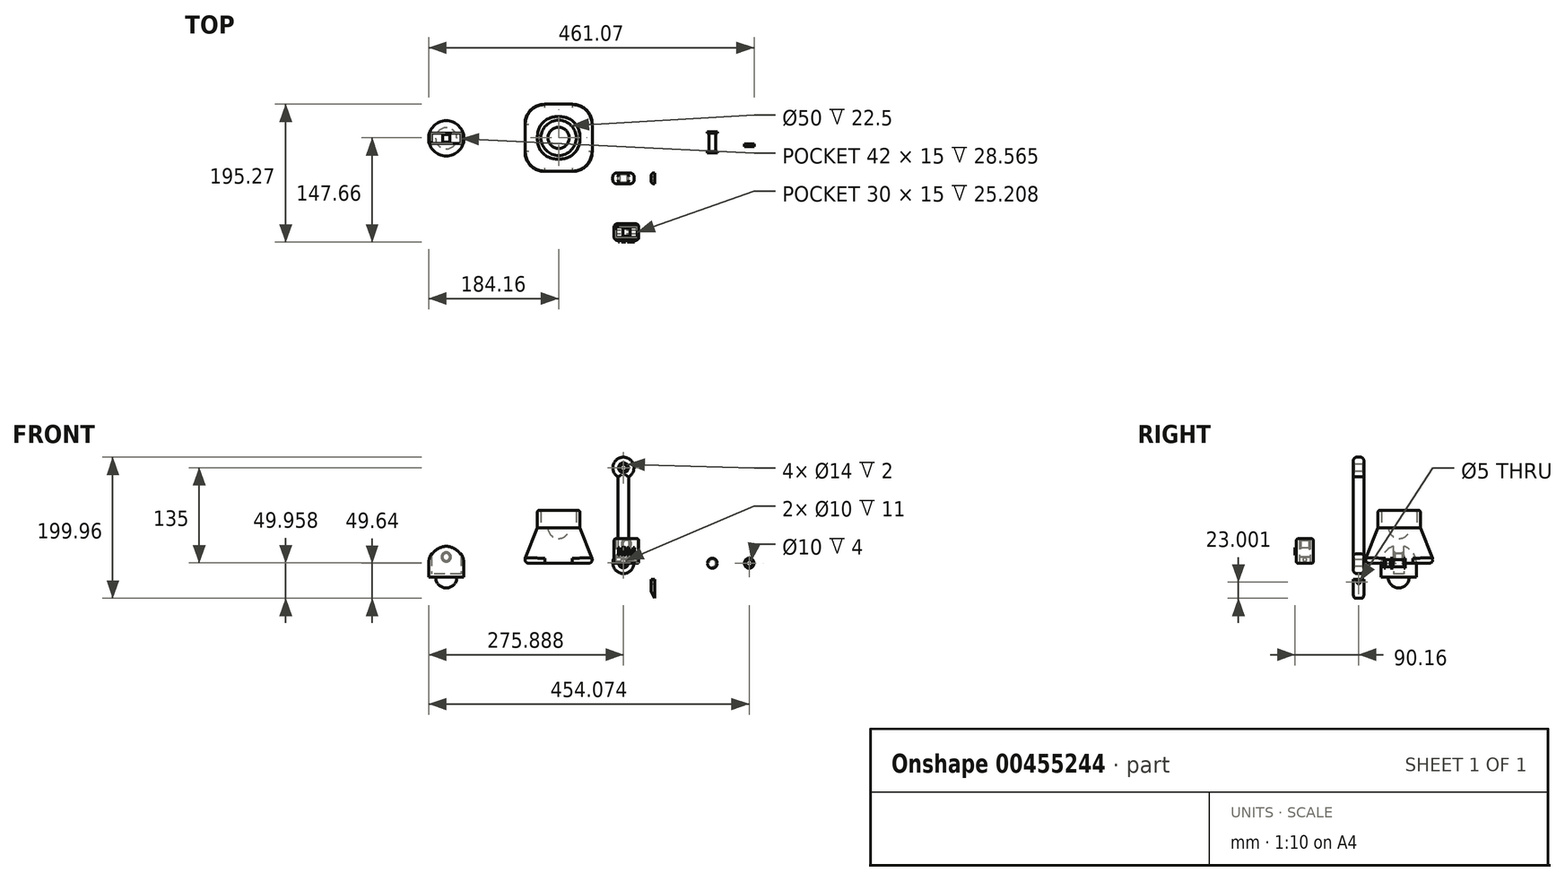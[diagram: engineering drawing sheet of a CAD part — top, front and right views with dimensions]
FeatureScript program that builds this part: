
annotation { "Feature Type Name" : "Feature", "Feature Type Description" : "" }
export const myFeature = defineFeature(function(context is Context, id is Id, definition is map)
    precondition{}
    {
        {
            var Q0;
            Q0=qCreatedBy(makeId("Top.planeOp"),FACE);
            var sketch = newSketch(context, id + "F0", { "sketchPlane" : qUnion([Q0])});
            skLineSegment(sketch, "E0.bottom", {"start": v(0, 0) * mm, "end": v(100, 0) * mm});
            skLineSegment(sketch, "E0.top", {"start": v(0, 100) * mm, "end": v(100, 100) * mm});
            skLineSegment(sketch, "E0.left", {"start": v(0, 0) * mm, "end": v(0, 100) * mm});
            skLineSegment(sketch, "E0.right", {"start": v(100, 0) * mm, "end": v(100, 100) * mm});
            skSolve(sketch);
        }
        {
            var Q0;
            Q0=makeQuery(id+"F0.imprint","IMPRINT",FACE,{"disambiguationData":[TD([[makeQuery(id+"F0.imprint","IMPRINT",EDGE,{"derivedFrom":sQuery(id+"F0.wireOp",EDGE,"E0.bottom")}),1.0]])]});
            cPlane(context, id + "F1", {"entities" : qUnion([Q0]), "cplaneType" : CPlaneType.OFFSET, "offset" : 50 * mm, "width" : 150 * mm, "height" : 150 * mm});
        }
        {
            var Q0;
            Q0=qCreatedBy(id+"F1.planeOp",FACE);
            var sketch = newSketch(context, id + "F2", { "sketchPlane" : qUnion([Q0])});
            skLineSegment(sketch, "E1.bottom", {"start": v(20, 80) * mm, "end": v(80, 80) * mm});
            skLineSegment(sketch, "E1.top", {"start": v(20, 20) * mm, "end": v(80, 20) * mm});
            skLineSegment(sketch, "E1.left", {"start": v(20, 80) * mm, "end": v(20, 20) * mm});
            skLineSegment(sketch, "E1.right", {"start": v(80, 80) * mm, "end": v(80, 20) * mm});
            skSolve(sketch);
        }
        {
            var Q0;
            Q0=makeQuery(id+"F0.imprint","IMPRINT",FACE,{"disambiguationData":[TD([[makeQuery(id+"F0.imprint","IMPRINT",EDGE,{"derivedFrom":sQuery(id+"F0.wireOp",EDGE,"E0.bottom")}),1.0]])]});
            var Q1;
            Q1=makeQuery(id+"F2.imprint","IMPRINT",FACE,{"disambiguationData":[TD([[makeQuery(id+"F2.imprint","IMPRINT",EDGE,{"derivedFrom":sQuery(id+"F2.wireOp",EDGE,"E1.bottom")}),-1.0]])]});
            loft(context, id + "F3", {"sheetProfilesArray" : [{ "sheetProfileEntities" : qUnion([Q0]) }, { "sheetProfileEntities" : qUnion([Q1]) }]});
        }
        {
            var Q0;
            Q0=makeQuery(id+"F3.opLoft","CAP_FACE",FACE,{"disambiguationData":[OSD([makeQuery(id+"F2.imprint","IMPRINT",FACE,{"disambiguationData":[TD([[makeQuery(id+"F2.imprint","IMPRINT",EDGE,{"derivedFrom":sQuery(id+"F2.wireOp",EDGE,"E1.bottom")}),-1.0]])]})])],"isStart":true});
            var sketch = newSketch(context, id + "F4", { "sketchPlane" : qUnion([Q0])});
            skLineSegment(sketch, "E2", {"start": v(50, 65) * mm, "end": v(50, 35) * mm});
            skArc(sketch, "E3", {"start": v(50, 35) * mm, "mid": v(65, 50) * mm, "end": v(50, 65) * mm});
            skPoint(sketch, "E4.orphan", {"position": v(50, 80) * mm});
            skPoint(sketch, "E5.orphan", {"position": v(50, 20) * mm});
            skSolve(sketch);
        }
        {
            var Q0;
            Q0=makeQuery(id+"F4.imprint","IMPRINT",FACE,{"disambiguationData":[TD([[makeQuery(id+"F4.imprint","IMPRINT",EDGE,{"derivedFrom":sQuery(id+"F4.wireOp",EDGE,"E2")}),1.0]])]});
            var Q1;
            Q1=sQuery(id+"F4.wireOp",EDGE,"E2");
            revolve(context, id + "F5", {"operationType" : NewBodyOperationType.REMOVE, "entities" : qUnion([Q0]), "axis" : qUnion([Q1]), "revolveType" : RevolveType.FULL, "oppositeDirection" : true});
        }
        {
            var Q0;
            Q0=makeQuery(id+"F3.opLoft","CAP_FACE",FACE,{"disambiguationData":[OSD([makeQuery(id+"F0.imprint","IMPRINT",FACE,{"disambiguationData":[TD([[makeQuery(id+"F0.imprint","IMPRINT",EDGE,{"derivedFrom":sQuery(id+"F0.wireOp",EDGE,"E0.bottom")}),1.0]])]})])],"isStart":true});
            fillet(context, id + "F6", {"entities" : qUnion([Q0]), "radius" : 5 * mm, "tangentPropagation" : true, "allowEdgeOverflow" : false});
        }
        {
            var Q0;
            Q0=makeQuery(id+"F3.opLoft","SWEPT_EDGE",EDGE,{"disambiguationData":[OSD([sQuery(id+"F0.wireOp",EDGE,"E0.bottom"),sQuery(id+"F0.wireOp",EDGE,"E0.right"),sQuery(id+"F2.wireOp",EDGE,"E1.top"),sQuery(id+"F2.wireOp",EDGE,"E1.right")])]});
            var Q1;
            Q1=makeQuery(id+"F3.opLoft","SWEPT_EDGE",EDGE,{"disambiguationData":[OSD([sQuery(id+"F0.wireOp",EDGE,"E0.top"),sQuery(id+"F0.wireOp",EDGE,"E0.right"),sQuery(id+"F2.wireOp",EDGE,"E1.bottom"),sQuery(id+"F2.wireOp",EDGE,"E1.right")])]});
            var Q2;
            Q2=makeQuery(id+"F3.opLoft","SWEPT_EDGE",EDGE,{"disambiguationData":[OSD([sQuery(id+"F0.wireOp",EDGE,"E0.top"),sQuery(id+"F0.wireOp",EDGE,"E0.left"),sQuery(id+"F2.wireOp",EDGE,"E1.bottom"),sQuery(id+"F2.wireOp",EDGE,"E1.left")])]});
            var Q3;
            Q3=makeQuery(id+"F3.opLoft","SWEPT_EDGE",EDGE,{"disambiguationData":[OSD([sQuery(id+"F0.wireOp",EDGE,"E0.bottom"),sQuery(id+"F0.wireOp",EDGE,"E0.left"),sQuery(id+"F2.wireOp",EDGE,"E1.top"),sQuery(id+"F2.wireOp",EDGE,"E1.left")])]});
            fillet(context, id + "F7", {"entities" : qUnion([Q0, Q1, Q2, Q3]), "radius" : 30 * mm, "tangentPropagation" : true, "allowEdgeOverflow" : false});
        }
        {
            var Q0;
            Q0=qCreatedBy(makeId("Top.planeOp"),FACE);
            var sketch = newSketch(context, id + "F8", { "sketchPlane" : qUnion([Q0])});
            skArc(sketch, "E6", {"start": v(184.89, 22.61) * mm, "mid": v(199.89, 37.61) * mm, "end": v(184.89, 52.61) * mm});
            skLineSegment(sketch, "E7", {"start": v(184.89, 22.61) * mm, "end": v(184.89, 52.61) * mm});
            skSolve(sketch);
        }
        {
            var Q0;
            Q0=qCreatedBy(makeId("Top.planeOp"),FACE);
            cPlane(context, id + "F9", {"entities" : qUnion([Q0]), "cplaneType" : CPlaneType.OFFSET, "offset" : 10 * mm, "width" : 150 * mm, "height" : 150 * mm});
        }
        {
            var Q0;
            Q0=qCreatedBy(id+"F9.planeOp",FACE);
            var sketch = newSketch(context, id + "F10", { "sketchPlane" : qUnion([Q0])});
            skLineSegment(sketch, "E8.bottom", {"start": v(177.39, 45.11) * mm, "end": v(192.39, 45.11) * mm});
            skLineSegment(sketch, "E8.top", {"start": v(177.39, 30.11) * mm, "end": v(192.39, 30.11) * mm});
            skLineSegment(sketch, "E8.left", {"start": v(177.39, 45.11) * mm, "end": v(177.39, 30.11) * mm});
            skLineSegment(sketch, "E8.right", {"start": v(192.39, 45.11) * mm, "end": v(192.39, 30.11) * mm});
            skSolve(sketch);
        }
        {
            var Q0;
            Q0=makeQuery(id+"F8.imprint","IMPRINT",FACE,{"disambiguationData":[TD([[makeQuery(id+"F8.imprint","IMPRINT",EDGE,{"derivedFrom":sQuery(id+"F8.wireOp",EDGE,"E6")}),1.0]])]});
            var Q1;
            Q1=sQuery(id+"F8.wireOp",EDGE,"E7");
            revolve(context, id + "F11", {"entities" : qUnion([Q0]), "axis" : qUnion([Q1]), "revolveType" : RevolveType.FULL});
        }
        {
            var Q0;
            Q0=qSketchRegion(id+"F10",true);
            extrude(context, id + "F12", {"entities" : qUnion([Q0]), "operationType" : NewBodyOperationType.ADD, "depth" : 120 * mm});
        }
        {
            var Q0;
            Q0=makeQuery(id+"F12.boolean.opBoolean","INTERSECT",EDGE,{"derivedFrom":[makeQuery(id+"F11.opRevolve","SWEPT_FACE",FACE,{"disambiguationData":[OSD([sQuery(id+"F8.wireOp",EDGE,"E6")])]}),makeQuery(id+"F12.opExtrude","SWEPT_FACE",FACE,{"disambiguationData":[OSD([sQuery(id+"F10.wireOp",EDGE,"E8.right")])]})]});
            var Q1;
            Q1=makeQuery(id+"F12.boolean.opBoolean","INTERSECT",EDGE,{"derivedFrom":[makeQuery(id+"F11.opRevolve","SWEPT_FACE",FACE,{"disambiguationData":[OSD([sQuery(id+"F8.wireOp",EDGE,"E6")])]}),makeQuery(id+"F12.opExtrude","SWEPT_FACE",FACE,{"disambiguationData":[OSD([sQuery(id+"F10.wireOp",EDGE,"E8.top")])]})]});
            var Q2;
            Q2=makeQuery(id+"F12.boolean.opBoolean","INTERSECT",EDGE,{"derivedFrom":[makeQuery(id+"F11.opRevolve","SWEPT_FACE",FACE,{"disambiguationData":[OSD([sQuery(id+"F8.wireOp",EDGE,"E6")])]}),makeQuery(id+"F12.opExtrude","SWEPT_FACE",FACE,{"disambiguationData":[OSD([sQuery(id+"F10.wireOp",EDGE,"E8.bottom")])]})]});
            var Q3;
            Q3=makeQuery(id+"F12.boolean.opBoolean","INTERSECT",EDGE,{"derivedFrom":[makeQuery(id+"F11.opRevolve","SWEPT_FACE",FACE,{"disambiguationData":[OSD([sQuery(id+"F8.wireOp",EDGE,"E6")])]}),makeQuery(id+"F12.opExtrude","SWEPT_FACE",FACE,{"disambiguationData":[OSD([sQuery(id+"F10.wireOp",EDGE,"E8.left")])]})]});
            var Q4;
            Q4=makeQuery(id+"F12.opExtrude","SWEPT_EDGE",EDGE,{"disambiguationData":[OSD([sQuery(id+"F10.wireOp",EDGE,"E8.bottom"),sQuery(id+"F10.wireOp",EDGE,"E8.left")])]});
            var Q5;
            Q5=makeQuery(id+"F12.opExtrude","SWEPT_EDGE",EDGE,{"disambiguationData":[OSD([sQuery(id+"F10.wireOp",EDGE,"E8.bottom"),sQuery(id+"F10.wireOp",EDGE,"E8.right")])]});
            var Q6;
            Q6=makeQuery(id+"F12.opExtrude","SWEPT_EDGE",EDGE,{"disambiguationData":[OSD([sQuery(id+"F10.wireOp",EDGE,"E8.top"),sQuery(id+"F10.wireOp",EDGE,"E8.right")])]});
            var Q7;
            Q7=makeQuery(id+"F12.opExtrude","SWEPT_EDGE",EDGE,{"disambiguationData":[OSD([sQuery(id+"F10.wireOp",EDGE,"E8.top"),sQuery(id+"F10.wireOp",EDGE,"E8.left")])]});
            fillet(context, id + "F13", {"entities" : qUnion([Q0, Q1, Q2, Q3, Q4, Q5, Q6, Q7]), "radius" : 5 * mm, "tangentPropagation" : true, "allowEdgeOverflow" : false});
        }
        {
            var Q0;
            Q0=makeQuery(id+"F12.opExtrude","CAP_EDGE",EDGE,{"disambiguationData":[OSD([sQuery(id+"F10.wireOp",EDGE,"E8.right")])],"isStart":false});
            cPoint(context, id + "F14", {"entities" : qUnion([Q0]), "parameter" : 0.5});
        }
        {
            var Q0;
            Q0=makeQuery(id+"F12.opExtrude","CAP_EDGE",EDGE,{"disambiguationData":[OSD([sQuery(id+"F10.wireOp",EDGE,"E8.left")])],"isStart":false});
            cPoint(context, id + "F15", {"entities" : qUnion([Q0]), "parameter" : 0.5});
        }
        {
            var Q0;
            {var subQ0=makeQuery(id+"F12.opExtrude","SWEPT_FACE",FACE,{"disambiguationData":[OSD([sQuery(id+"F10.wireOp",EDGE,"E8.left")])]});Q0=makeQuery(id+"F13.opFillet","BLEND_EDGE",EDGE,{"blendedFrom":[makeQuery(id+"F12.boolean.opBoolean","INTERSECT",EDGE,{"derivedFrom":[makeQuery(id+"F11.opRevolve","SWEPT_FACE",FACE,{"disambiguationData":[OSD([sQuery(id+"F8.wireOp",EDGE,"E6")])]}),subQ0]}),subQ0],"blendedInto":[subQ0]});}
            cPoint(context, id + "F16", {"entities" : qUnion([Q0]), "parameter" : 0.5});
        }
        {
            var Q0;
            Q0=qCreatedBy(id+"F14",VERTEX);
            var Q1;
            Q1=qCreatedBy(id+"F15",VERTEX);
            var Q2;
            Q2=qCreatedBy(id+"F16",VERTEX);
            cPlane(context, id + "F17", {"entities" : qUnion([Q0, Q1, Q2]), "cplaneType" : CPlaneType.THREE_POINT, "offset" : 25 * mm, "width" : 150 * mm, "height" : 150 * mm});
        }
        {
            var Q0;
            Q0=qCreatedBy(id+"F17.planeOp",FACE);
            var sketch = newSketch(context, id + "F18", { "sketchPlane" : qUnion([Q0])});
            skCircle(sketch, "E9", {"center": v(-184.89, 137.5) * mm, "radius": 15 * mm});
            skSolve(sketch);
        }
        {
            var Q0;
            Q0=makeQuery(id+"F18.imprint","IMPRINT",FACE,{"disambiguationData":[TD([[makeQuery(id+"F18.imprint","IMPRINT",EDGE,{"derivedFrom":sQuery(id+"F18.wireOp",EDGE,"E9")}),1.0]])]});
            extrude(context, id + "F19", {"entities" : qUnion([Q0]), "operationType" : NewBodyOperationType.ADD, "endBound" : BoundingType.SYMMETRIC, "depth" : 15 * mm, "offsetDistance" : 25 * mm});
        }
        {
            var Q0;
            Q0=makeQuery(id+"F19.opExtrude","CAP_EDGE",EDGE,{"disambiguationData":[OSD([sQuery(id+"F18.wireOp",EDGE,"E9")])],"isStart":true});
            var Q1;
            Q1=makeQuery(id+"F19.opExtrude","CAP_EDGE",EDGE,{"disambiguationData":[OSD([sQuery(id+"F18.wireOp",EDGE,"E9")])],"isStart":false});
            fillet(context, id + "F20", {"entities" : qUnion([Q0, Q1]), "radius" : 5 * mm, "tangentPropagation" : true, "allowEdgeOverflow" : false});
        }
        {
            var Q0;
            Q0=makeQuery(id+"F19.boolean.opBoolean","MERGE",FACE,{"derivedFrom":[makeQuery(id+"F12.opExtrude","SWEPT_FACE",FACE,{"disambiguationData":[OSD([sQuery(id+"F10.wireOp",EDGE,"E8.top")])]}),makeQuery(id+"F19.opExtrude","CAP_FACE",FACE,{"disambiguationData":[OSD([sQuery(id+"F18.wireOp",EDGE,"E9")])],"isStart":true})]});
            var sketch = newSketch(context, id + "F21", { "sketchPlane" : qUnion([Q0])});
            skCircle(sketch, "E10", {"center": v(184.89, 137.5) * mm, "radius": 5 * mm});
            skCircle(sketch, "E11", {"center": v(184.89, 137.5) * mm, "radius": 7 * mm});
            skSolve(sketch);
        }
        {
            var Q0;
            Q0=sQuery(id+"F21.wireOp",VERTEX,"E10.center");
            var Q1;
            Q1=makeQuery(id+"F11.opRevolve","SWEPT_BODY",BODY,{"disambiguationData":[OSD([sQuery(id+"F8.wireOp",EDGE,"E6"),sQuery(id+"F8.wireOp",EDGE,"E7")])]});
            hole(context, id + "F22", {"style" : HoleStyle.SIMPLE, "endStyle" : HoleEndStyle.THROUGH, "holeDiameter" : 10 * mm, "tappedDepth" : 12 * mm, "tapClearance" : 3, "locations" : qUnion([Q0]), "scope" : qUnion([Q1])});
        }
        {
            var Q0;
            Q0=makeQuery(id+"F19.boolean.opBoolean","MERGE",FACE,{"derivedFrom":[makeQuery(id+"F12.opExtrude","SWEPT_FACE",FACE,{"disambiguationData":[OSD([sQuery(id+"F10.wireOp",EDGE,"E8.bottom")])]}),makeQuery(id+"F19.opExtrude","CAP_FACE",FACE,{"disambiguationData":[OSD([sQuery(id+"F18.wireOp",EDGE,"E9")])],"isStart":false})]});
            var sketch = newSketch(context, id + "F23", { "sketchPlane" : qUnion([Q0])});
            skCircle(sketch, "E12", {"center": v(-184.89, 137.5) * mm, "radius": 7 * mm});
            skSolve(sketch);
        }
        {
            var Q0;
            Q0=qSketchRegion(id+"F21",true);
            var Q1;
            Q1=qSketchRegion(id+"F23",true);
            extrude(context, id + "F24", {"entities" : qUnion([Q0, Q1]), "operationType" : NewBodyOperationType.REMOVE, "oppositeDirection" : true, "depth" : 2 * mm, "hasSecondDirection" : true, "secondDirectionOppositeDirection" : false, "secondDirectionDepth" : 2 * mm});
        }
        {
            var Q0;
            Q0=qCreatedBy(makeId("Top.planeOp"),FACE);
            var sketch = newSketch(context, id + "F25", { "sketchPlane" : qUnion([Q0])});
            skLineSegment(sketch, "E13.bottom", {"start": v(267.71, 58.7) * mm, "end": v(272.71, 58.7) * mm});
            skLineSegment(sketch, "E13.top", {"start": v(267.71, 28.7) * mm, "end": v(272.71, 28.7) * mm});
            skLineSegment(sketch, "E13.left", {"start": v(267.71, 58.7) * mm, "end": v(267.71, 28.7) * mm});
            skLineSegment(sketch, "E13.right", {"start": v(272.71, 56.7) * mm, "end": v(272.71, 30.7) * mm});
            skLineSegment(sketch, "E14.bottom", {"start": v(272.71, 58.7) * mm, "end": v(274.71, 58.7) * mm});
            skLineSegment(sketch, "E14.top", {"start": v(272.71, 56.7) * mm, "end": v(274.71, 56.7) * mm});
            skLineSegment(sketch, "E14.right", {"start": v(274.71, 58.7) * mm, "end": v(274.71, 56.7) * mm});
            skLineSegment(sketch, "E15.bottom", {"start": v(272.71, 28.7) * mm, "end": v(274.71, 28.7) * mm});
            skLineSegment(sketch, "E15.top", {"start": v(272.71, 30.7) * mm, "end": v(274.71, 30.7) * mm});
            skLineSegment(sketch, "E15.right", {"start": v(274.71, 28.7) * mm, "end": v(274.71, 30.7) * mm});
            skSolve(sketch);
        }
        {
            var Q0;
            Q0=makeQuery(id+"F25.imprint","IMPRINT",FACE,{"disambiguationData":[TD([[makeQuery(id+"F25.imprint","IMPRINT",EDGE,{"derivedFrom":sQuery(id+"F25.wireOp",EDGE,"E13.bottom")}),-1.0]])]});
            var Q1;
            Q1=sQuery(id+"F25.wireOp",EDGE,"E13.left");
            revolve(context, id + "F26", {"entities" : qUnion([Q0]), "axis" : qUnion([Q1]), "revolveType" : RevolveType.FULL});
        }
        {
            var Q0;
            Q0=qCreatedBy(id+"F17.planeOp",FACE);
            var sketch = newSketch(context, id + "F27", { "sketchPlane" : qUnion([Q0])});
            skCircle(sketch, "E16", {"center": v(-319.91, 0) * mm, "radius": 7 * mm});
            skCircle(sketch, "E17", {"center": v(-319.91, 0) * mm, "radius": 5 * mm});
            skSolve(sketch);
        }
        {
            var Q0;
            Q0=qSketchRegion(id+"F27",true);
            extrude(context, id + "F28", {"entities" : qUnion([Q0]), "depth" : 4 * mm});
        }
        {
            var Q0;
            Q0=qCreatedBy(makeId("Top.planeOp"),FACE);
            var sketch = newSketch(context, id + "F29", { "sketchPlane" : qUnion([Q0])});
            skArc(sketch, "E18", {"start": v(-109.16, 24.23) * mm, "mid": v(-84.16, 49.23) * mm, "end": v(-109.16, 74.23) * mm});
            skLineSegment(sketch, "E19", {"start": v(-109.16, 74.23) * mm, "end": v(-109.16, 24.23) * mm});
            skSolve(sketch);
        }
        {
            var Q0;
            Q0=makeQuery(id+"F29.imprint","IMPRINT",FACE,{"disambiguationData":[TD([[makeQuery(id+"F29.imprint","IMPRINT",EDGE,{"derivedFrom":sQuery(id+"F29.wireOp",EDGE,"E18")}),1.0]])]});
            var Q1;
            Q1=sQuery(id+"F29.wireOp",EDGE,"E19");
            revolve(context, id + "F30", {"entities" : qUnion([Q0]), "axis" : qUnion([Q1]), "revolveType" : RevolveType.ONE_DIRECTION, "angle" : 180 * degree});
        }
        {
            var Q0;
            Q0=qCreatedBy(makeId("Front.planeOp"),FACE);
            var sketch = newSketch(context, id + "F31", { "sketchPlane" : qUnion([Q0])});
            skLineSegment(sketch, "E20.left", {"start": v(134.23, 122.33) * mm, "end": v(134.23, 13.3) * mm});
            skLineSegment(sketch, "E20.right", {"start": v(149.23, 122.33) * mm, "end": v(149.23, 13.3) * mm});
            skArc(sketch, "E21", {"start": v(149.23, 122.33) * mm, "mid": v(141.73, 150.32) * mm, "end": v(134.23, 122.33) * mm});
            skArc(sketch, "E22", {"start": v(134.23, 13.3) * mm, "mid": v(141.73, -14.68) * mm, "end": v(149.23, 13.3) * mm});
            skSolve(sketch);
        }
        {
            var Q0;
            Q0=makeQuery(id+"F31.imprint","IMPRINT",FACE,{"disambiguationData":[TD([[makeQuery(id+"F31.imprint","IMPRINT",EDGE,{"derivedFrom":sQuery(id+"F31.wireOp",EDGE,"E20.left")}),1.0]])]});
            extrude(context, id + "F32", {"entities" : qUnion([Q0]), "depth" : 15 * mm});
        }
        {
            var Q0;
            Q0=makeQuery(id+"F32.opExtrude","CAP_FACE",FACE,{"disambiguationData":[OSD([sQuery(id+"F31.wireOp",EDGE,"E20.left"),sQuery(id+"F31.wireOp",EDGE,"E20.right"),sQuery(id+"F31.wireOp",EDGE,"E21"),sQuery(id+"F31.wireOp",EDGE,"E22")])],"isStart":false});
            var Q1;
            Q1=makeQuery(id+"F32.opExtrude","CAP_FACE",FACE,{"disambiguationData":[OSD([sQuery(id+"F31.wireOp",EDGE,"E20.left"),sQuery(id+"F31.wireOp",EDGE,"E20.right"),sQuery(id+"F31.wireOp",EDGE,"E21"),sQuery(id+"F31.wireOp",EDGE,"E22")])],"isStart":true});
            fillet(context, id + "F33", {"entities" : qUnion([Q0, Q1]), "radius" : 5 * mm, "tangentPropagation" : true, "allowEdgeOverflow" : false});
        }
        {
            var Q0;
            Q0=makeQuery(id+"F32.opExtrude","CAP_FACE",FACE,{"disambiguationData":[OSD([sQuery(id+"F31.wireOp",EDGE,"E20.left"),sQuery(id+"F31.wireOp",EDGE,"E20.right"),sQuery(id+"F31.wireOp",EDGE,"E21"),sQuery(id+"F31.wireOp",EDGE,"E22")])],"isStart":false});
            var sketch = newSketch(context, id + "F34", { "sketchPlane" : qUnion([Q0])});
            skCircle(sketch, "E23", {"center": v(141.73, 135.32) * mm, "radius": 5 * mm});
            skCircle(sketch, "E24", {"center": v(141.73, 0.32) * mm, "radius": 5 * mm});
            skCircle(sketch, "E25", {"center": v(141.73, 135.32) * mm, "radius": 7 * mm});
            skCircle(sketch, "E26", {"center": v(141.73, 0.32) * mm, "radius": 7 * mm});
            skSolve(sketch);
        }
        {
            var Q0;
            Q0=makeQuery(id+"F34.imprint","IMPRINT",FACE,{"disambiguationData":[TD([[makeQuery(id+"F34.imprint","IMPRINT",EDGE,{"derivedFrom":sQuery(id+"F34.wireOp",EDGE,"E23")}),1.0]])]});
            var Q1;
            Q1=makeQuery(id+"F34.imprint","IMPRINT",FACE,{"disambiguationData":[TD([[makeQuery(id+"F34.imprint","IMPRINT",EDGE,{"derivedFrom":sQuery(id+"F34.wireOp",EDGE,"E24")}),1.0]])]});
            extrude(context, id + "F35", {"entities" : qUnion([Q0, Q1]), "operationType" : NewBodyOperationType.REMOVE, "endBound" : BoundingType.THROUGH_ALL, "oppositeDirection" : true, "depth" : 25 * mm});
        }
        {
            var Q0;
            Q0=qSketchRegion(id+"F34",true);
            extrude(context, id + "F36", {"entities" : qUnion([Q0]), "operationType" : NewBodyOperationType.REMOVE, "oppositeDirection" : true, "depth" : 2 * mm});
        }
        {
            var Q0;
            Q0=makeQuery(id+"F32.opExtrude","CAP_FACE",FACE,{"disambiguationData":[OSD([sQuery(id+"F31.wireOp",EDGE,"E20.left"),sQuery(id+"F31.wireOp",EDGE,"E20.right"),sQuery(id+"F31.wireOp",EDGE,"E21"),sQuery(id+"F31.wireOp",EDGE,"E22")])],"isStart":true});
            var sketch = newSketch(context, id + "F37", { "sketchPlane" : qUnion([Q0])});
            skCircle(sketch, "E27", {"center": v(-141.73, 135.32) * mm, "radius": 7 * mm});
            skCircle(sketch, "E28", {"center": v(-141.73, 0.32) * mm, "radius": 7 * mm});
            skSolve(sketch);
        }
        {
            var Q0;
            Q0=qSketchRegion(id+"F37",true);
            extrude(context, id + "F38", {"entities" : qUnion([Q0]), "operationType" : NewBodyOperationType.REMOVE, "oppositeDirection" : true, "depth" : 2 * mm});
        }
        {
            var Q0;
            Q0=makeQuery(id+"F30.opRevolve","CAP_FACE",FACE,{"disambiguationData":[OSD([sQuery(id+"F29.wireOp",EDGE,"E18"),sQuery(id+"F29.wireOp",EDGE,"E19")])],"isStart":true});
            var sketch = newSketch(context, id + "F39", { "sketchPlane" : qUnion([Q0])});
            skLineSegment(sketch, "E29.bottom", {"start": v(-88.16, -56.73) * mm, "end": v(-130.16, -56.73) * mm});
            skLineSegment(sketch, "E29.top", {"start": v(-88.16, -41.73) * mm, "end": v(-130.16, -41.73) * mm});
            skLineSegment(sketch, "E29.left", {"start": v(-88.16, -56.73) * mm, "end": v(-88.16, -41.73) * mm});
            skLineSegment(sketch, "E29.right", {"start": v(-130.16, -56.73) * mm, "end": v(-130.16, -41.73) * mm});
            skSolve(sketch);
        }
        {
            var Q0;
            Q0=makeQuery(id+"F39.imprint","IMPRINT",FACE,{"disambiguationData":[TD([[makeQuery(id+"F39.imprint","IMPRINT",EDGE,{"derivedFrom":sQuery(id+"F39.wireOp",EDGE,"E29.bottom")}),1.0]])]});
            var Q1;
            Q1=makeQuery(id+"F39.imprint","IMPRINT",FACE,{"disambiguationData":[TD([[makeQuery(id+"F39.imprint","IMPRINT",EDGE,{"derivedFrom":sQuery(id+"F39.wireOp",EDGE,"E29.bottom")}),-1.0]])]});
            extrude(context, id + "F40", {"entities" : qUnion([Q0, Q1]), "operationType" : NewBodyOperationType.ADD, "depth" : 20 * mm});
        }
        {
            var Q0;
            Q0=makeQuery(id+"F40.opExtrude","CAP_FACE",FACE,{"disambiguationData":[OSD([sQuery(id+"F29.wireOp",EDGE,"E18")])],"isStart":false});
            var sketch = newSketch(context, id + "F41", { "sketchPlane" : qUnion([Q0])});
            skArc(sketch, "E30", {"start": v(-109.16, -34.23) * mm, "mid": v(-124.16, -49.23) * mm, "end": v(-109.16, -64.23) * mm});
            skLineSegment(sketch, "E31", {"start": v(-109.16, -64.23) * mm, "end": v(-109.16, -34.23) * mm});
            skSolve(sketch);
        }
        {
            var Q0;
            Q0=makeQuery(id+"F41.imprint","IMPRINT",FACE,{"disambiguationData":[TD([[makeQuery(id+"F41.imprint","IMPRINT",EDGE,{"derivedFrom":sQuery(id+"F41.wireOp",EDGE,"E30")}),1.0]])]});
            var Q1;
            Q1=sQuery(id+"F41.wireOp",EDGE,"E31");
            revolve(context, id + "F42", {"operationType" : NewBodyOperationType.ADD, "entities" : qUnion([Q0]), "axis" : qUnion([Q1]), "revolveType" : RevolveType.FULL});
        }
        {
            var Q0;
            Q0=qSketchRegion(id+"F39",true);
            extrude(context, id + "F43", {"entities" : qUnion([Q0]), "operationType" : NewBodyOperationType.REMOVE, "endBound" : BoundingType.THROUGH_ALL, "oppositeDirection" : true, "depth" : 25 * mm, "hasSecondDirection" : true, "secondDirectionOppositeDirection" : false, "secondDirectionDepth" : 15 * mm});
        }
        {
            var Q0;
            Q0=makeQuery(id+"F43.boolean.opBoolean","COPY",FACE,{"derivedFrom":makeQuery(id+"F43.opExtrude","SWEPT_FACE",FACE,{"disambiguationData":[OSD([sQuery(id+"F39.wireOp",EDGE,"E29.top")])]})});
            var sketch = newSketch(context, id + "F44", { "sketchPlane" : qUnion([Q0])});
            skCircle(sketch, "E32", {"center": v(109.16, 8.85) * mm, "radius": 7 * mm});
            skPoint(sketch, "E32.centerSnap0", {"position": v(109.16, 23.85) * mm});
            skPoint(sketch, "E32.centerSnap1", {"position": v(130.16, -1.85) * mm});
            skSolve(sketch);
        }
        {
            var Q0;
            Q0=makeQuery(id+"F44.imprint","IMPRINT",FACE,{"disambiguationData":[TD([[makeQuery(id+"F44.imprint","IMPRINT",EDGE,{"derivedFrom":sQuery(id+"F44.wireOp",EDGE,"E32")}),1.0]])]});
            extrude(context, id + "F45", {"entities" : qUnion([Q0]), "operationType" : NewBodyOperationType.ADD, "depth" : 2 * mm});
        }
        {
            var Q0;
            Q0=makeQuery(id+"F45.opExtrude","CAP_FACE",FACE,{"disambiguationData":[OSD([sQuery(id+"F44.wireOp",EDGE,"E32")])],"isStart":false});
            var sketch = newSketch(context, id + "F46", { "sketchPlane" : qUnion([Q0])});
            skCircle(sketch, "E33", {"center": v(109.16, 8.85) * mm, "radius": 5 * mm});
            skSolve(sketch);
        }
        {
            var Q0;
            Q0=makeQuery(id+"F46.imprint","IMPRINT",FACE,{"disambiguationData":[TD([[makeQuery(id+"F46.imprint","IMPRINT",EDGE,{"derivedFrom":sQuery(id+"F46.wireOp",EDGE,"E33")}),1.0]])]});
            extrude(context, id + "F47", {"entities" : qUnion([Q0]), "operationType" : NewBodyOperationType.ADD, "endBound" : BoundingType.UP_TO_NEXT, "depth" : 25 * mm});
        }
        {
            var Q0;
            Q0=qCreatedBy(makeId("Top.planeOp"),FACE);
            var sketch = newSketch(context, id + "F48", { "sketchPlane" : qUnion([Q0])});
            skLineSegment(sketch, "E34.bottom", {"start": v(203.21, -84.7) * mm, "end": v(208.21, -84.7) * mm});
            skLineSegment(sketch, "E34.top", {"start": v(203.21, -99.7) * mm, "end": v(208.21, -99.7) * mm});
            skLineSegment(sketch, "E34.left", {"start": v(198.21, -89.7) * mm, "end": v(198.21, -94.7) * mm});
            skLineSegment(sketch, "E34.right", {"start": v(213.21, -89.7) * mm, "end": v(213.21, -94.7) * mm});
            skPoint(sketch, "E35.visualSharp", {"position": v(198.21, -84.7) * mm});
            skArc(sketch, "E35.filletArc", {"start": v(203.21, -84.7) * mm, "mid": v(199.68, -86.16) * mm, "end": v(198.21, -89.7) * mm});
            skPoint(sketch, "E36.visualSharp", {"position": v(213.21, -84.7) * mm});
            skArc(sketch, "E36.filletArc", {"start": v(213.21, -89.7) * mm, "mid": v(211.75, -86.16) * mm, "end": v(208.21, -84.7) * mm});
            skPoint(sketch, "E37.visualSharp", {"position": v(213.21, -99.7) * mm});
            skArc(sketch, "E37.filletArc", {"start": v(208.21, -99.7) * mm, "mid": v(211.75, -98.23) * mm, "end": v(213.21, -94.7) * mm});
            skPoint(sketch, "E38.visualSharp", {"position": v(198.21, -99.7) * mm});
            skArc(sketch, "E38.filletArc", {"start": v(198.21, -94.7) * mm, "mid": v(199.68, -98.23) * mm, "end": v(203.21, -99.7) * mm});
            skLineSegment(sketch, "E39.bottom", {"start": v(192.71, -74.2) * mm, "end": v(218.71, -74.2) * mm});
            skLineSegment(sketch, "E39.top", {"start": v(192.71, -110.2) * mm, "end": v(218.71, -110.2) * mm});
            skLineSegment(sketch, "E39.left", {"start": v(187.71, -79.2) * mm, "end": v(187.71, -105.2) * mm});
            skLineSegment(sketch, "E39.right", {"start": v(223.71, -79.2) * mm, "end": v(223.71, -105.2) * mm});
            skPoint(sketch, "E40.visualSharp", {"position": v(187.71, -74.2) * mm});
            skArc(sketch, "E40.filletArc", {"start": v(192.71, -74.2) * mm, "mid": v(189.18, -75.66) * mm, "end": v(187.71, -79.2) * mm});
            skPoint(sketch, "E41.visualSharp", {"position": v(223.71, -74.2) * mm});
            skArc(sketch, "E41.filletArc", {"start": v(223.71, -79.2) * mm, "mid": v(222.25, -75.66) * mm, "end": v(218.71, -74.2) * mm});
            skPoint(sketch, "E42.visualSharp", {"position": v(223.71, -110.2) * mm});
            skArc(sketch, "E42.filletArc", {"start": v(218.71, -110.2) * mm, "mid": v(222.25, -108.73) * mm, "end": v(223.71, -105.2) * mm});
            skPoint(sketch, "E43.visualSharp", {"position": v(187.71, -110.2) * mm});
            skArc(sketch, "E43.filletArc", {"start": v(187.71, -105.2) * mm, "mid": v(189.18, -108.73) * mm, "end": v(192.71, -110.2) * mm});
            skSolve(sketch);
        }
        {
            var Q0;
            Q0=makeQuery(id+"F48.imprint","IMPRINT",FACE,{"disambiguationData":[TD([[makeQuery(id+"F48.imprint","IMPRINT",EDGE,{"derivedFrom":sQuery(id+"F48.wireOp",EDGE,"E34.bottom")}),1.0]])]});
            extrude(context, id + "F49", {"entities" : qUnion([Q0]), "depth" : 20 * mm});
        }
        {
            var Q0;
            Q0=makeQuery(id+"F49.opExtrude","CAP_EDGE",EDGE,{"disambiguationData":[OSD([sQuery(id+"F48.wireOp",EDGE,"E39.left")])],"isStart":false});
            fillet(context, id + "F50", {"entities" : qUnion([Q0]), "radius" : 10 * mm, "tangentPropagation" : true, "allowEdgeOverflow" : false});
        }
        {
            var Q0;
            Q0=makeQuery(id+"F49.opExtrude","CAP_EDGE",EDGE,{"disambiguationData":[OSD([sQuery(id+"F48.wireOp",EDGE,"E34.top")])],"isStart":true});
            var Q1;
            Q1=makeQuery(id+"F49.opExtrude","CAP_EDGE",EDGE,{"disambiguationData":[OSD([sQuery(id+"F48.wireOp",EDGE,"E37.filletArc")])],"isStart":true});
            fillet(context, id + "F51", {"entities" : qUnion([Q0, Q1]), "radius" : 5 * mm, "tangentPropagation" : true, "allowEdgeOverflow" : false});
        }
        {
            var Q0;
            Q0=makeQuery(id+"F11.opRevolve","SWEPT_BODY",BODY,{"disambiguationData":[OSD([sQuery(id+"F8.wireOp",EDGE,"E6"),sQuery(id+"F8.wireOp",EDGE,"E7")])]});
            deleteBodies(context, id + "F52", {"entities" : qUnion([Q0])});
        }
        {
            var Q0;
            Q0=makeQuery(id+"F49.opExtrude","SWEPT_BODY",BODY,{"disambiguationData":[OSD([sQuery(id+"F48.wireOp",EDGE,"E34.bottom"),sQuery(id+"F48.wireOp",EDGE,"E34.top"),sQuery(id+"F48.wireOp",EDGE,"E34.left"),sQuery(id+"F48.wireOp",EDGE,"E34.right"),sQuery(id+"F48.wireOp",EDGE,"E35.filletArc"),sQuery(id+"F48.wireOp",EDGE,"E36.filletArc"),sQuery(id+"F48.wireOp",EDGE,"E37.filletArc"),sQuery(id+"F48.wireOp",EDGE,"E38.filletArc"),sQuery(id+"F48.wireOp",EDGE,"E39.bottom"),sQuery(id+"F48.wireOp",EDGE,"E39.top"),sQuery(id+"F48.wireOp",EDGE,"E39.left"),sQuery(id+"F48.wireOp",EDGE,"E39.right"),sQuery(id+"F48.wireOp",EDGE,"E40.filletArc"),sQuery(id+"F48.wireOp",EDGE,"E41.filletArc"),sQuery(id+"F48.wireOp",EDGE,"E42.filletArc"),sQuery(id+"F48.wireOp",EDGE,"E43.filletArc")])]});
            deleteBodies(context, id + "F53", {"entities" : qUnion([Q0])});
        }
        {
            var Q0;
            Q0=makeQuery(id+"F43.boolean.opBoolean","COPY",FACE,{"derivedFrom":makeQuery(id+"F43.opExtrude","SWEPT_FACE",FACE,{"disambiguationData":[OSD([sQuery(id+"F39.wireOp",EDGE,"E29.bottom")])]})});
            var sketch = newSketch(context, id + "F54", { "sketchPlane" : qUnion([Q0])});
            skCircle(sketch, "E44", {"center": v(-109.16, 8.85) * mm, "radius": 7 * mm});
            skSolve(sketch);
        }
        {
            var Q0;
            Q0=makeQuery(id+"F54.imprint","IMPRINT",FACE,{"disambiguationData":[TD([[makeQuery(id+"F54.imprint","IMPRINT",EDGE,{"derivedFrom":sQuery(id+"F54.wireOp",EDGE,"E44")}),1.0]])]});
            extrude(context, id + "F55", {"entities" : qUnion([Q0]), "operationType" : NewBodyOperationType.ADD, "depth" : 2 * mm});
        }
        {
            var Q0;
            Q0=qCreatedBy(makeId("Top.planeOp"),FACE);
            var sketch = newSketch(context, id + "F56", { "sketchPlane" : qUnion([Q0])});
            skLineSegment(sketch, "E45.bottom", {"start": v(133.56, -71.66) * mm, "end": v(158.56, -71.66) * mm});
            skLineSegment(sketch, "E45.top", {"start": v(133.56, -95.66) * mm, "end": v(158.56, -95.66) * mm});
            skLineSegment(sketch, "E45.left", {"start": v(128.56, -76.66) * mm, "end": v(128.56, -90.66) * mm});
            skLineSegment(sketch, "E45.right", {"start": v(163.56, -76.66) * mm, "end": v(163.56, -90.66) * mm});
            skPoint(sketch, "E46.visualSharp", {"position": v(163.56, -71.66) * mm});
            skArc(sketch, "E46.filletArc", {"start": v(163.56, -76.66) * mm, "mid": v(162.1, -73.13) * mm, "end": v(158.56, -71.66) * mm});
            skPoint(sketch, "E47.visualSharp", {"position": v(163.56, -95.66) * mm});
            skArc(sketch, "E47.filletArc", {"start": v(158.56, -95.66) * mm, "mid": v(162.1, -94.2) * mm, "end": v(163.56, -90.66) * mm});
            skPoint(sketch, "E48.visualSharp", {"position": v(128.56, -95.66) * mm});
            skArc(sketch, "E48.filletArc", {"start": v(128.56, -90.66) * mm, "mid": v(130.03, -94.2) * mm, "end": v(133.56, -95.66) * mm});
            skPoint(sketch, "E49.visualSharp", {"position": v(128.56, -71.66) * mm});
            skArc(sketch, "E49.filletArc", {"start": v(133.56, -71.66) * mm, "mid": v(130.03, -73.13) * mm, "end": v(128.56, -76.66) * mm});
            skPoint(sketch, "E50.firstSnap0", {"position": v(146.06, -71.66) * mm});
            skLineSegment(sketch, "E50.bottom", {"start": v(131.06, -76.16) * mm, "end": v(161.06, -76.16) * mm});
            skLineSegment(sketch, "E50.top", {"start": v(131.06, -91.16) * mm, "end": v(161.06, -91.16) * mm});
            skLineSegment(sketch, "E50.left", {"start": v(131.06, -76.16) * mm, "end": v(131.06, -91.16) * mm});
            skLineSegment(sketch, "E50.right", {"start": v(161.06, -76.16) * mm, "end": v(161.06, -91.16) * mm});
            skSolve(sketch);
        }
        {
            var Q0;
            Q0=makeQuery(id+"F56.imprint","IMPRINT",FACE,{"disambiguationData":[TD([[makeQuery(id+"F56.imprint","IMPRINT",EDGE,{"derivedFrom":sQuery(id+"F56.wireOp",EDGE,"E45.bottom")}),-1.0]])]});
            extrude(context, id + "F57", {"entities" : qUnion([Q0]), "depth" : 35 * mm});
        }
        {
            var Q0;
            Q0=makeQuery(id+"F57.opExtrude","SWEPT_FACE",FACE,{"disambiguationData":[OSD([sQuery(id+"F56.wireOp",EDGE,"E50.bottom")])]});
            var sketch = newSketch(context, id + "F58", { "sketchPlane" : qUnion([Q0])});
            skCircle(sketch, "E51", {"center": v(146.06, 27.5) * mm, "radius": 5 * mm});
            skCircle(sketch, "E52", {"center": v(146.06, 27.5) * mm, "radius": 7 * mm});
            skSolve(sketch);
        }
        {
            var Q0;
            Q0=makeQuery(id+"F58.imprint","IMPRINT",FACE,{"disambiguationData":[TD([[makeQuery(id+"F58.imprint","IMPRINT",EDGE,{"derivedFrom":sQuery(id+"F58.wireOp",EDGE,"E51")}),1.0]])]});
            extrude(context, id + "F59", {"entities" : qUnion([Q0]), "operationType" : NewBodyOperationType.ADD, "endBound" : BoundingType.UP_TO_NEXT, "depth" : 25 * mm});
        }
        {
            var Q0;
            Q0=makeQuery(id+"F58.imprint","IMPRINT",FACE,{"disambiguationData":[TD([[makeQuery(id+"F58.imprint","IMPRINT",EDGE,{"derivedFrom":sQuery(id+"F58.wireOp",EDGE,"E51")}),-1.0]])]});
            extrude(context, id + "F60", {"entities" : qUnion([Q0]), "operationType" : NewBodyOperationType.ADD, "depth" : 2 * mm});
        }
        {
            var Q0;
            Q0=makeQuery(id+"F57.opExtrude","SWEPT_FACE",FACE,{"disambiguationData":[OSD([sQuery(id+"F56.wireOp",EDGE,"E50.top")])]});
            var sketch = newSketch(context, id + "F61", { "sketchPlane" : qUnion([Q0])});
            skCircle(sketch, "E53", {"center": v(-146.06, 27.5) * mm, "radius": 7 * mm});
            skSolve(sketch);
        }
        {
            var Q0;
            Q0=makeQuery(id+"F61.imprint","IMPRINT",FACE,{"disambiguationData":[TD([[makeQuery(id+"F61.imprint","IMPRINT",EDGE,{"derivedFrom":sQuery(id+"F61.wireOp",EDGE,"E53")}),1.0]])]});
            extrude(context, id + "F62", {"entities" : qUnion([Q0]), "operationType" : NewBodyOperationType.ADD, "depth" : 2 * mm});
        }
        {
            var Q0;
            Q0=qCreatedBy(makeId("Front.planeOp"),FACE);
            var sketch = newSketch(context, id + "F63", { "sketchPlane" : qUnion([Q0])});
            skLineSegment(sketch, "E54", {"start": v(181.27, -22.64) * mm, "end": v(181.27, -40.64) * mm});
            skLineSegment(sketch, "E55", {"start": v(181.27, -40.64) * mm, "end": v(186.27, -49.64) * mm});
            skLineSegment(sketch, "E56", {"start": v(186.27, -49.64) * mm, "end": v(186.27, -22.64) * mm});
            skLineSegment(sketch, "E57", {"start": v(186.27, -22.64) * mm, "end": v(181.27, -22.64) * mm});
            skSolve(sketch);
        }
        {
            var Q0;
            Q0=makeQuery(id+"F63.imprint","IMPRINT",FACE,{"disambiguationData":[TD([[makeQuery(id+"F63.imprint","IMPRINT",EDGE,{"derivedFrom":sQuery(id+"F63.wireOp",EDGE,"E54")}),1.0]])]});
            extrude(context, id + "F64", {"entities" : qUnion([Q0]), "depth" : 15 * mm});
        }
        {
            var Q0;
            Q0=makeQuery(id+"F57.opExtrude","SWEPT_FACE",FACE,{"disambiguationData":[OSD([sQuery(id+"F56.wireOp",EDGE,"E50.left")])]});
            var sketch = newSketch(context, id + "F65", { "sketchPlane" : qUnion([Q0])});
            skCircle(sketch, "E58", {"center": v(-83.66, 5) * mm, "radius": 2.5 * mm});
            skPoint(sketch, "E58.centerSnap0", {"position": v(-83.66, 0) * mm});
            skLineSegment(sketch, "E59.bottom", {"start": v(-91.16, 9.75) * mm, "end": v(-76.16, 9.75) * mm});
            skLineSegment(sketch, "E59.top", {"start": v(-91.16, 9) * mm, "end": v(-76.16, 9) * mm});
            skLineSegment(sketch, "E59.left", {"start": v(-91.16, 9.75) * mm, "end": v(-91.16, 9) * mm});
            skLineSegment(sketch, "E59.right", {"start": v(-76.16, 9.75) * mm, "end": v(-76.16, 9) * mm});
            skSolve(sketch);
        }
        {
            var Q0;
            Q0=makeQuery(id+"F65.imprint","IMPRINT",FACE,{"disambiguationData":[TD([[makeQuery(id+"F65.imprint","IMPRINT",EDGE,{"derivedFrom":sQuery(id+"F65.wireOp",EDGE,"E58")}),1.0]])]});
            var Q1;
            Q1=makeQuery(id+"F65.imprint","IMPRINT",FACE,{"disambiguationData":[TD([[makeQuery(id+"F65.imprint","IMPRINT",EDGE,{"derivedFrom":sQuery(id+"F65.wireOp",EDGE,"E59.bottom")}),-1.0]])]});
            extrude(context, id + "F66", {"entities" : qUnion([Q0, Q1]), "operationType" : NewBodyOperationType.ADD, "endBound" : BoundingType.UP_TO_NEXT, "depth" : 25 * mm});
        }
        {
            var Q0;
            Q0=makeQuery(id+"F64.opExtrude","SWEPT_FACE",FACE,{"disambiguationData":[OSD([sQuery(id+"F63.wireOp",EDGE,"E56")])]});
            var sketch = newSketch(context, id + "F67", { "sketchPlane" : qUnion([Q0])});
            skCircle(sketch, "E60", {"center": v(-7.5, -26.64) * mm, "radius": 2.5 * mm});
            skPoint(sketch, "E60.centerSnap0", {"position": v(-7.5, -22.64) * mm});
            skSolve(sketch);
        }
        {
            var Q0;
            Q0=makeQuery(id+"F67.imprint","IMPRINT",FACE,{"disambiguationData":[TD([[makeQuery(id+"F67.imprint","IMPRINT",EDGE,{"derivedFrom":sQuery(id+"F67.wireOp",EDGE,"E60")}),1.0]])]});
            extrude(context, id + "F68", {"entities" : qUnion([Q0]), "operationType" : NewBodyOperationType.REMOVE, "endBound" : BoundingType.UP_TO_NEXT, "oppositeDirection" : true, "depth" : 25 * mm});
        }
        {
            var Q0;
            Q0=makeQuery(id+"F57.opExtrude","CAP_EDGE",EDGE,{"disambiguationData":[OSD([sQuery(id+"F56.wireOp",EDGE,"E45.top")])],"isStart":true});
            var Q1;
            Q1=makeQuery(id+"F57.opExtrude","CAP_EDGE",EDGE,{"disambiguationData":[OSD([sQuery(id+"F56.wireOp",EDGE,"E45.right")])],"isStart":true});
            var Q2;
            Q2=makeQuery(id+"F57.opExtrude","CAP_EDGE",EDGE,{"disambiguationData":[OSD([sQuery(id+"F56.wireOp",EDGE,"E47.filletArc")])],"isStart":true});
            var Q3;
            Q3=makeQuery(id+"F57.opExtrude","CAP_EDGE",EDGE,{"disambiguationData":[OSD([sQuery(id+"F56.wireOp",EDGE,"E45.bottom")])],"isStart":true});
            var Q4;
            Q4=makeQuery(id+"F57.opExtrude","CAP_EDGE",EDGE,{"disambiguationData":[OSD([sQuery(id+"F56.wireOp",EDGE,"E49.filletArc")])],"isStart":true});
            var Q5;
            Q5=makeQuery(id+"F57.opExtrude","CAP_EDGE",EDGE,{"disambiguationData":[OSD([sQuery(id+"F56.wireOp",EDGE,"E45.left")])],"isStart":true});
            var Q6;
            Q6=makeQuery(id+"F57.opExtrude","CAP_EDGE",EDGE,{"disambiguationData":[OSD([sQuery(id+"F56.wireOp",EDGE,"E48.filletArc")])],"isStart":true});
            var Q7;
            Q7=makeQuery(id+"F57.opExtrude","CAP_EDGE",EDGE,{"disambiguationData":[OSD([sQuery(id+"F56.wireOp",EDGE,"E46.filletArc")])],"isStart":true});
            fillet(context, id + "F69", {"entities" : qUnion([Q0, Q1, Q2, Q3, Q4, Q5, Q6, Q7]), "radius" : 2 * mm, "tangentPropagation" : true, "allowEdgeOverflow" : false});
        }
        {
            var Q0;
            Q0=makeQuery(id+"F57.opExtrude","CAP_EDGE",EDGE,{"disambiguationData":[OSD([sQuery(id+"F56.wireOp",EDGE,"E45.top")])],"isStart":false});
            var Q1;
            Q1=makeQuery(id+"F57.opExtrude","CAP_EDGE",EDGE,{"disambiguationData":[OSD([sQuery(id+"F56.wireOp",EDGE,"E46.filletArc")])],"isStart":false});
            var Q2;
            Q2=makeQuery(id+"F57.opExtrude","CAP_EDGE",EDGE,{"disambiguationData":[OSD([sQuery(id+"F56.wireOp",EDGE,"E47.filletArc")])],"isStart":false});
            var Q3;
            Q3=makeQuery(id+"F57.opExtrude","CAP_EDGE",EDGE,{"disambiguationData":[OSD([sQuery(id+"F56.wireOp",EDGE,"E48.filletArc")])],"isStart":false});
            var Q4;
            Q4=makeQuery(id+"F57.opExtrude","CAP_EDGE",EDGE,{"disambiguationData":[OSD([sQuery(id+"F56.wireOp",EDGE,"E45.left")])],"isStart":false});
            var Q5;
            Q5=makeQuery(id+"F57.opExtrude","CAP_EDGE",EDGE,{"disambiguationData":[OSD([sQuery(id+"F56.wireOp",EDGE,"E45.bottom")])],"isStart":false});
            var Q6;
            Q6=makeQuery(id+"F57.opExtrude","CAP_EDGE",EDGE,{"disambiguationData":[OSD([sQuery(id+"F56.wireOp",EDGE,"E49.filletArc")])],"isStart":false});
            fillet(context, id + "F70", {"entities" : qUnion([Q0, Q1, Q2, Q3, Q4, Q5, Q6]), "radius" : 3 * mm, "tangentPropagation" : true, "allowEdgeOverflow" : false});
        }
        {
            var Q0;
            Q0=makeQuery(id+"F64.opExtrude","CAP_EDGE",EDGE,{"disambiguationData":[OSD([sQuery(id+"F63.wireOp",EDGE,"E55")])],"isStart":false});
            var Q1;
            Q1=makeQuery(id+"F64.opExtrude","CAP_EDGE",EDGE,{"disambiguationData":[OSD([sQuery(id+"F63.wireOp",EDGE,"E55")])],"isStart":true});
            var Q2;
            Q2=makeQuery(id+"F64.opExtrude","SWEPT_EDGE",EDGE,{"disambiguationData":[OSD([sQuery(id+"F63.wireOp",EDGE,"E54"),sQuery(id+"F63.wireOp",EDGE,"E55")])]});
            var Q3;
            Q3=makeQuery(id+"F64.opExtrude","CAP_EDGE",EDGE,{"disambiguationData":[OSD([sQuery(id+"F63.wireOp",EDGE,"E54")])],"isStart":false});
            var Q4;
            Q4=makeQuery(id+"F64.opExtrude","CAP_EDGE",EDGE,{"disambiguationData":[OSD([sQuery(id+"F63.wireOp",EDGE,"E54")])],"isStart":true});
            fillet(context, id + "F71", {"entities" : qUnion([Q0, Q1, Q2, Q3, Q4]), "radius" : 3 * mm, "tangentPropagation" : true, "allowEdgeOverflow" : false});
        }
        {
            var Q0;
            Q0=makeQuery(id+"F3.opLoft","CAP_FACE",FACE,{"disambiguationData":[OSD([makeQuery(id+"F2.imprint","IMPRINT",FACE,{"disambiguationData":[TD([[makeQuery(id+"F2.imprint","IMPRINT",EDGE,{"derivedFrom":sQuery(id+"F2.wireOp",EDGE,"E1.bottom")}),-1.0]])]})])],"isStart":true});
            var sketch = newSketch(context, id + "F72", { "sketchPlane" : qUnion([Q0])});
            skCircle(sketch, "E61", {"center": v(50, 50) * mm, "radius": 25 * mm});
            skSolve(sketch);
        }
        {
            var Q0;
            Q0=makeQuery(id+"F72.imprint","IMPRINT",FACE,{"disambiguationData":[TD([[makeQuery(id+"F72.imprint","IMPRINT",EDGE,{"derivedFrom":sQuery(id+"F72.wireOp",EDGE,"E61")}),-1.0]])]});
            extrude(context, id + "F73", {"entities" : qUnion([Q0]), "operationType" : NewBodyOperationType.ADD, "depth" : 25 * mm});
        }
        {
            var Q0;
            {var subQ0=sQuery(id+"F2.wireOp",EDGE,"E1.bottom");var subQ1=sQuery(id+"F2.wireOp",EDGE,"E1.top");var subQ2=sQuery(id+"F2.wireOp",EDGE,"E1.left");var subQ3=sQuery(id+"F2.wireOp",EDGE,"E1.right");Q0=makeQuery(id+"F73.opExtrude","CAP_FACE",FACE,{"disambiguationData":[OSD([sQuery(id+"F0.wireOp",EDGE,"E0.bottom"),sQuery(id+"F0.wireOp",EDGE,"E0.top"),sQuery(id+"F0.wireOp",EDGE,"E0.left"),sQuery(id+"F0.wireOp",EDGE,"E0.right"),subQ0,subQ1,subQ2,subQ3,makeQuery(id+"F2.imprint","IMPRINT",FACE,{"disambiguationData":[TD([[makeQuery(id+"F2.imprint","IMPRINT",EDGE,{"derivedFrom":subQ0}),-1.0]])]}),sQuery(id+"F72.wireOp",EDGE,"E61")])],"isStart":false});}
            fillet(context, id + "F74", {"entities" : qUnion([Q0]), "radius" : 2.5 * mm, "tangentPropagation" : true, "allowEdgeOverflow" : false});
        }
        {
            var Q0;
            Q0=makeQuery(id+"F57.opExtrude","SWEPT_FACE",FACE,{"disambiguationData":[OSD([sQuery(id+"F56.wireOp",EDGE,"E45.top")])]});
            var sketch = newSketch(context, id + "F75", { "sketchPlane" : qUnion([Q0])});
            skText(sketch, "E62", { "text": "IEM\n\n", "fontName": "OpenSans-Regular.ttf"});
            const initialGuessF75  = {"E62": [0.13356, 0.01172, 1, 0, 0.01056]};
            skSetInitialGuess(sketch, initialGuessF75);
            skSolve(sketch);
        }
        {
            var Q0;
            Q0=qSketchRegion(id+"F75",true);
            extrude(context, id + "F76", {"entities" : qUnion([Q0]), "operationType" : NewBodyOperationType.ADD, "depth" : 2 * mm});
        }
    });
